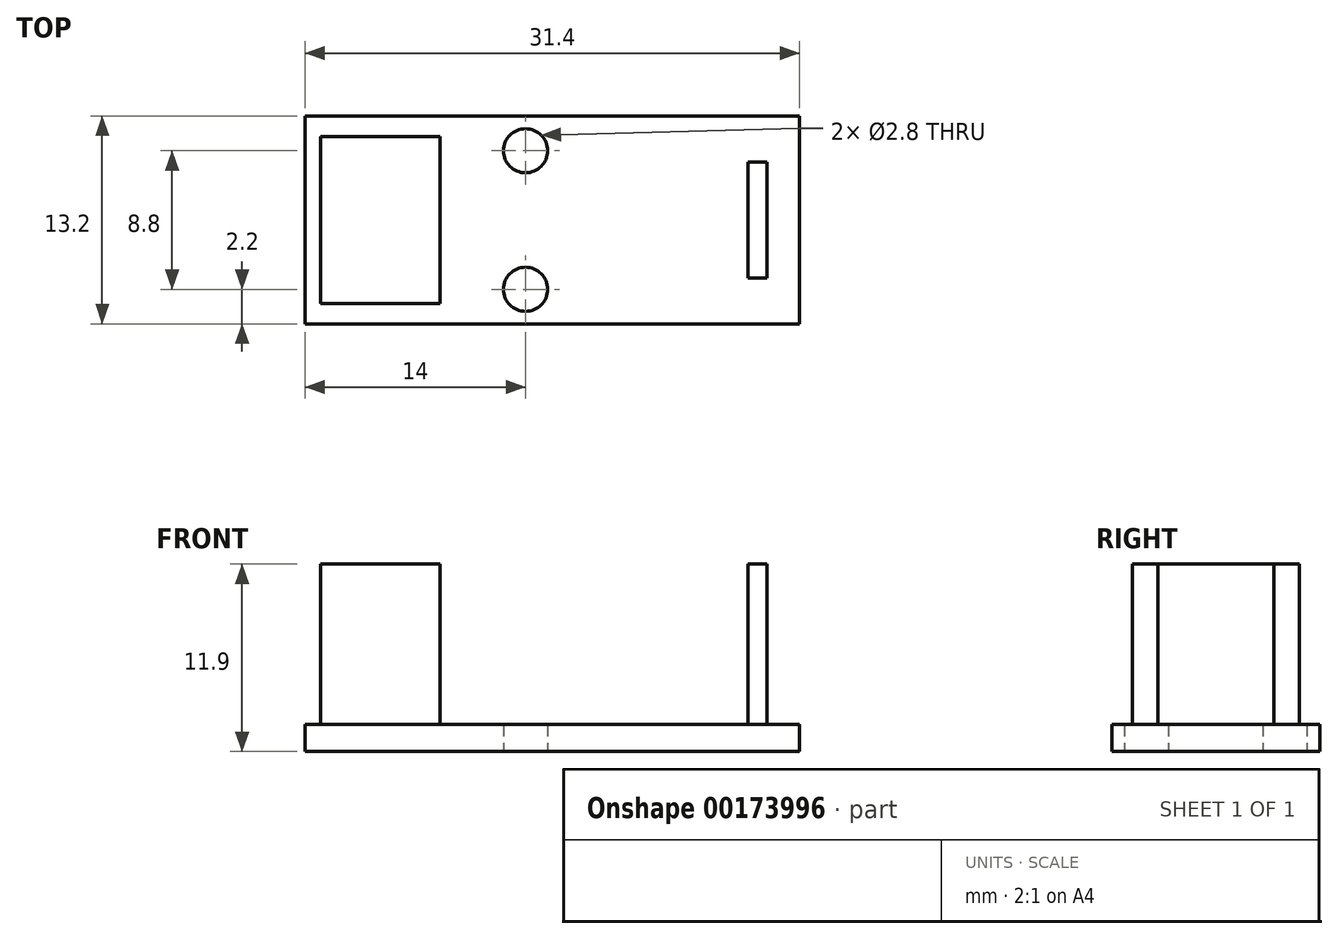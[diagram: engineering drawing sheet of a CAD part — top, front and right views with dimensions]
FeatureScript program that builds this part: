
annotation { "Feature Type Name" : "Feature", "Feature Type Description" : "" }
export const myFeature = defineFeature(function(context is Context, id is Id, definition is map)
    precondition{}
    {
        {
            var Q0;
            Q0=qCreatedBy(makeId("Top.planeOp"),FACE);
            var sketch = newSketch(context, id + "F0", { "sketchPlane" : qUnion([Q0])});
            skLineSegment(sketch, "E0.bottom", {"start": v(15.7, 6.6) * mm, "end": v(-15.7, 6.6) * mm});
            skLineSegment(sketch, "E0.top", {"start": v(15.7, -6.6) * mm, "end": v(-15.7, -6.6) * mm});
            skLineSegment(sketch, "E0.left", {"start": v(15.7, 6.6) * mm, "end": v(15.7, -6.6) * mm});
            skLineSegment(sketch, "E0.right", {"start": v(-15.7, 6.6) * mm, "end": v(-15.7, -6.6) * mm});
            skPoint(sketch, "E0.middle", {"position": v(0, 0) * mm});
            skCircle(sketch, "E1", {"center": v(-1.7, 4.4) * mm, "radius": 1.4 * mm});
            skCircle(sketch, "E2", {"center": v(-1.7, -4.4) * mm, "radius": 1.4 * mm});
            skLineSegment(sketch, "E3", {"start": v(-1.7, 3) * mm, "end": v(-1.7, -3) * mm, "construction": true});
            skPoint(sketch, "E4", {"position": v(-1.7, 0) * mm});
            skSolve(sketch);
        }
        {
            var Q0;
            Q0 = qSketchRegion(id + "F0", true);
            extrude(context, id + "F1", {"entities" : qUnion([Q0]), "depth" : 1.7 * mm});
        }
        {
            var Q0;
            Q0=makeQuery(id+"F1.opExtrude","CAP_FACE",FACE,{"disambiguationData":[OSD([sQuery(id+"F0.wireOp",EDGE,"E0.bottom"),sQuery(id+"F0.wireOp",EDGE,"E0.top"),sQuery(id+"F0.wireOp",EDGE,"E0.left"),sQuery(id+"F0.wireOp",EDGE,"E0.right"),sQuery(id+"F0.wireOp",EDGE,"E1"),sQuery(id+"F0.wireOp",EDGE,"E2")])],"isStart":false});
            var sketch = newSketch(context, id + "F2", { "sketchPlane" : qUnion([Q0])});
            skLineSegment(sketch, "E5.bottom", {"start": v(-7.12, 5.3) * mm, "end": v(-14.72, 5.3) * mm});
            skLineSegment(sketch, "E5.top", {"start": v(-7.12, -5.3) * mm, "end": v(-14.72, -5.3) * mm});
            skLineSegment(sketch, "E5.left", {"start": v(-7.12, 5.3) * mm, "end": v(-7.12, -5.3) * mm});
            skLineSegment(sketch, "E5.right", {"start": v(-14.72, 5.3) * mm, "end": v(-14.72, -5.3) * mm});
            skPoint(sketch, "E5.middle", {"position": v(-10.92, 0) * mm});
            skPoint(sketch, "E6", {"position": v(-15.7, 0) * mm});
            skLineSegment(sketch, "E7.bottom", {"start": v(13.62, 3.69) * mm, "end": v(12.42, 3.69) * mm});
            skLineSegment(sketch, "E7.top", {"start": v(13.62, -3.69) * mm, "end": v(12.42, -3.69) * mm});
            skLineSegment(sketch, "E7.left", {"start": v(13.62, 3.69) * mm, "end": v(13.62, -3.69) * mm});
            skLineSegment(sketch, "E7.right", {"start": v(12.42, 3.69) * mm, "end": v(12.42, -3.69) * mm});
            skPoint(sketch, "E7.middle", {"position": v(13.02, 0) * mm});
            skSolve(sketch);
        }
        {
            var Q0;
            Q0 = qSketchRegion(id + "F2", true);
            extrude(context, id + "F3", {"entities" : qUnion([Q0]), "operationType" : NewBodyOperationType.ADD, "depth" : 10.2 * mm});
        }
    });
